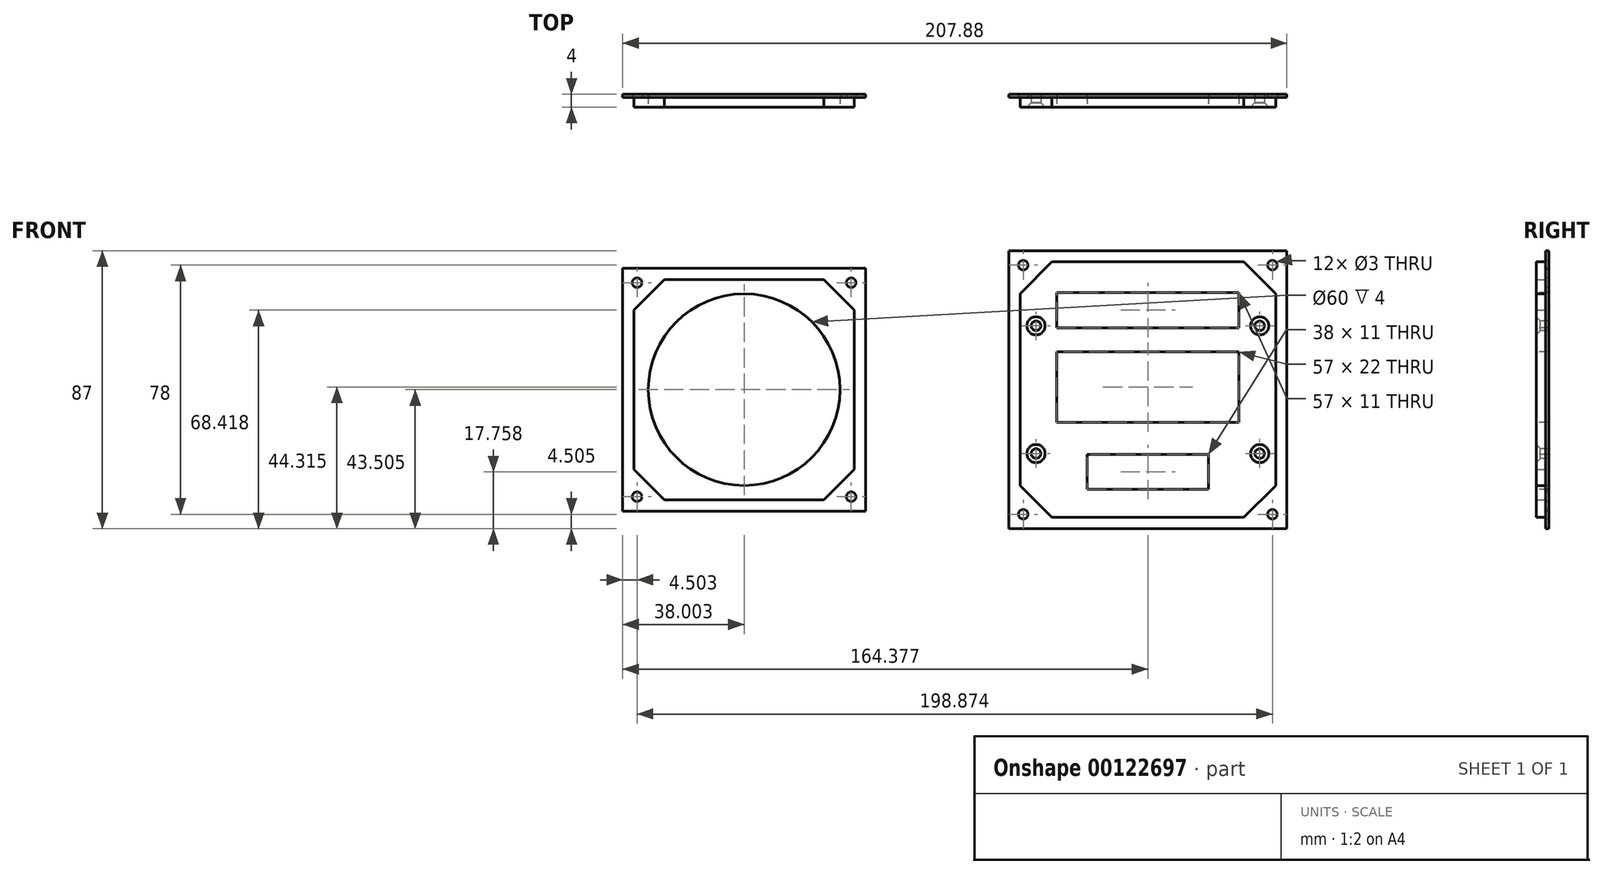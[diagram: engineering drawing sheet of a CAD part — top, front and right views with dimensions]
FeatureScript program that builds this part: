
annotation { "Feature Type Name" : "Feature", "Feature Type Description" : "" }
export const myFeature = defineFeature(function(context is Context, id is Id, definition is map)
    precondition{}
    {
        {
            var Q0;
            Q0=qCreatedBy(makeId("Front.planeOp"),FACE);
            cPlane(context, id + "F0", {"entities" : qUnion([Q0]), "cplaneType" : CPlaneType.OFFSET, "offset" : 5 * mm, "width" : 150 * mm, "height" : 150 * mm});
        }
        {
            var Q0;
            Q0=qCreatedBy(id+"F0.planeOp",FACE);
            var sketch = newSketch(context, id + "F1", { "sketchPlane" : qUnion([Q0])});
            skLineSegment(sketch, "E0.0", {"start": v(-61.26, 263.3) * mm, "end": v(-61.26, 238.3) * mm});
            skLineSegment(sketch, "E0.1", {"start": v(-61.26, 213.3) * mm, "end": v(-70.76, 203.8) * mm});
            skLineSegment(sketch, "E0.2", {"start": v(-70.76, 203.8) * mm, "end": v(-95.76, 203.8) * mm});
            skLineSegment(sketch, "E0.3", {"start": v(-120.76, 203.8) * mm, "end": v(-130.26, 213.3) * mm});
            skLineSegment(sketch, "E0.4", {"start": v(-130.26, 213.3) * mm, "end": v(-130.26, 238.3) * mm});
            skLineSegment(sketch, "E0.5", {"start": v(-130.26, 263.3) * mm, "end": v(-120.76, 272.8) * mm});
            skLineSegment(sketch, "E0.6", {"start": v(-120.76, 272.8) * mm, "end": v(-95.76, 272.8) * mm});
            skLineSegment(sketch, "E0.7", {"start": v(-70.76, 272.8) * mm, "end": v(-61.26, 263.3) * mm});
            skPoint(sketch, "E1", {"position": v(-95.76, 238.3) * mm});
            skLineSegment(sketch, "E2", {"start": v(-95.76, 272.8) * mm, "end": v(-70.76, 272.8) * mm});
            skLineSegment(sketch, "E3", {"start": v(-130.26, 238.3) * mm, "end": v(-130.26, 263.3) * mm});
            skLineSegment(sketch, "E4", {"start": v(-61.26, 238.3) * mm, "end": v(-61.26, 213.3) * mm});
            skLineSegment(sketch, "E5", {"start": v(-95.76, 203.8) * mm, "end": v(-120.76, 203.8) * mm});
            skSolve(sketch);
        }
        {
            var Q0;
            Q0=qSketchRegion(id+"F1",true);
            extrude(context, id + "F2", {"entities" : qUnion([Q0]), "depth" : 3 * mm});
        }
        {
            var Q0;
            Q0=makeQuery(id+"F2.opExtrude","CAP_FACE",FACE,{"disambiguationData":[OSD([sQuery(id+"F1.wireOp",EDGE,"E0.0"),sQuery(id+"F1.wireOp",EDGE,"E0.1"),sQuery(id+"F1.wireOp",EDGE,"E0.2"),sQuery(id+"F1.wireOp",EDGE,"E0.3"),sQuery(id+"F1.wireOp",EDGE,"E0.4"),sQuery(id+"F1.wireOp",EDGE,"E0.5"),sQuery(id+"F1.wireOp",EDGE,"E0.6"),sQuery(id+"F1.wireOp",EDGE,"E0.7"),sQuery(id+"F1.wireOp",EDGE,"E2"),sQuery(id+"F1.wireOp",EDGE,"E3"),sQuery(id+"F1.wireOp",EDGE,"E4"),sQuery(id+"F1.wireOp",EDGE,"E5")])],"isStart":true});
            var sketch = newSketch(context, id + "F3", { "sketchPlane" : qUnion([Q0])});
            skLineSegment(sketch, "E6.bottom", {"start": v(133.76, 276.3) * mm, "end": v(57.76, 276.3) * mm});
            skLineSegment(sketch, "E6.top", {"start": v(133.76, 200.3) * mm, "end": v(57.76, 200.3) * mm});
            skLineSegment(sketch, "E6.left", {"start": v(133.76, 276.3) * mm, "end": v(133.76, 200.3) * mm});
            skLineSegment(sketch, "E6.right", {"start": v(57.76, 276.3) * mm, "end": v(57.76, 200.3) * mm});
            skSolve(sketch);
        }
        {
            var Q0;
            Q0=qSketchRegion(id+"F3",true);
            extrude(context, id + "F4", {"entities" : qUnion([Q0]), "operationType" : NewBodyOperationType.ADD, "depth" : 1 * mm});
        }
        {
            var Q0;
            Q0=makeQuery(id+"F2.opExtrude","CAP_FACE",FACE,{"disambiguationData":[OSD([sQuery(id+"F1.wireOp",EDGE,"E0.0"),sQuery(id+"F1.wireOp",EDGE,"E0.1"),sQuery(id+"F1.wireOp",EDGE,"E0.2"),sQuery(id+"F1.wireOp",EDGE,"E0.3"),sQuery(id+"F1.wireOp",EDGE,"E0.4"),sQuery(id+"F1.wireOp",EDGE,"E0.5"),sQuery(id+"F1.wireOp",EDGE,"E0.6"),sQuery(id+"F1.wireOp",EDGE,"E0.7"),sQuery(id+"F1.wireOp",EDGE,"E2"),sQuery(id+"F1.wireOp",EDGE,"E3"),sQuery(id+"F1.wireOp",EDGE,"E4"),sQuery(id+"F1.wireOp",EDGE,"E5")])],"isStart":false});
            var sketch = newSketch(context, id + "F5", { "sketchPlane" : qUnion([Q0])});
            skCircle(sketch, "E7", {"center": v(-95.76, 238.3) * mm, "radius": 30 * mm});
            skCircle(sketch, "E8", {"center": v(-129.26, 271.8) * mm, "radius": 1.5 * mm});
            skCircle(sketch, "E9", {"center": v(-62.26, 271.8) * mm, "radius": 1.5 * mm});
            skCircle(sketch, "E10", {"center": v(-129.26, 204.8) * mm, "radius": 1.5 * mm});
            skCircle(sketch, "E11", {"center": v(-62.26, 204.8) * mm, "radius": 1.5 * mm});
            skSolve(sketch);
        }
        {
            var Q0;
            Q0=sQuery(id+"F5.wireOp",VERTEX,"E8.center");
            var Q1;
            Q1=sQuery(id+"F5.wireOp",VERTEX,"E9.center");
            var Q2;
            Q2=sQuery(id+"F5.wireOp",VERTEX,"E11.center");
            var Q3;
            Q3=sQuery(id+"F5.wireOp",VERTEX,"E10.center");
            var Q4;
            Q4=makeQuery(id+"F2.opExtrude","SWEPT_BODY",BODY,{"disambiguationData":[OSD([sQuery(id+"F1.wireOp",EDGE,"E0.0"),sQuery(id+"F1.wireOp",EDGE,"E0.1"),sQuery(id+"F1.wireOp",EDGE,"E0.2"),sQuery(id+"F1.wireOp",EDGE,"E0.3"),sQuery(id+"F1.wireOp",EDGE,"E0.4"),sQuery(id+"F1.wireOp",EDGE,"E0.5"),sQuery(id+"F1.wireOp",EDGE,"E0.6"),sQuery(id+"F1.wireOp",EDGE,"E0.7"),sQuery(id+"F1.wireOp",EDGE,"E2"),sQuery(id+"F1.wireOp",EDGE,"E3"),sQuery(id+"F1.wireOp",EDGE,"E4"),sQuery(id+"F1.wireOp",EDGE,"E5")])]});
            hole(context, id + "F6", {"style" : HoleStyle.SIMPLE, "endStyle" : HoleEndStyle.THROUGH, "holeDiameter" : 3 * mm, "locations" : qUnion([Q0, Q1, Q2, Q3]), "scope" : qUnion([Q4]), "isTappedThrough" : true});
        }
        {
            var Q0;
            Q0=sQuery(id+"F5.wireOp",VERTEX,"E7.center");
            var Q1;
            Q1=makeQuery(id+"F2.opExtrude","SWEPT_BODY",BODY,{"disambiguationData":[OSD([sQuery(id+"F1.wireOp",EDGE,"E0.0"),sQuery(id+"F1.wireOp",EDGE,"E0.1"),sQuery(id+"F1.wireOp",EDGE,"E0.2"),sQuery(id+"F1.wireOp",EDGE,"E0.3"),sQuery(id+"F1.wireOp",EDGE,"E0.4"),sQuery(id+"F1.wireOp",EDGE,"E0.5"),sQuery(id+"F1.wireOp",EDGE,"E0.6"),sQuery(id+"F1.wireOp",EDGE,"E0.7"),sQuery(id+"F1.wireOp",EDGE,"E2"),sQuery(id+"F1.wireOp",EDGE,"E3"),sQuery(id+"F1.wireOp",EDGE,"E4"),sQuery(id+"F1.wireOp",EDGE,"E5")])]});
            hole(context, id + "F7", {"style" : HoleStyle.SIMPLE, "endStyle" : HoleEndStyle.THROUGH, "holeDiameter" : 60 * mm, "locations" : qUnion([Q0]), "scope" : qUnion([Q1]), "isTappedThrough" : true});
        }
        {
            var Q0;
            Q0=qCreatedBy(id+"F0.planeOp",FACE);
            var sketch = newSketch(context, id + "F8", { "sketchPlane" : qUnion([Q0])});
            skLineSegment(sketch, "E12.0", {"start": v(70.62, 268.3) * mm, "end": v(70.62, 238.3) * mm});
            skLineSegment(sketch, "E12.1", {"start": v(70.62, 208.3) * mm, "end": v(60.62, 198.3) * mm});
            skLineSegment(sketch, "E12.2", {"start": v(60.62, 198.3) * mm, "end": v(30.62, 198.3) * mm});
            skLineSegment(sketch, "E12.3", {"start": v(0.62, 198.3) * mm, "end": v(-9.38, 208.3) * mm});
            skLineSegment(sketch, "E12.4", {"start": v(-9.38, 208.3) * mm, "end": v(-9.38, 238.3) * mm});
            skLineSegment(sketch, "E12.5", {"start": v(-9.38, 268.3) * mm, "end": v(0.62, 278.3) * mm});
            skLineSegment(sketch, "E12.6", {"start": v(0.62, 278.3) * mm, "end": v(30.62, 278.3) * mm});
            skLineSegment(sketch, "E12.7", {"start": v(60.62, 278.3) * mm, "end": v(70.62, 268.3) * mm});
            skPoint(sketch, "E13", {"position": v(30.62, 238.3) * mm});
            skLineSegment(sketch, "E14", {"start": v(30.62, 278.3) * mm, "end": v(60.62, 278.3) * mm});
            skLineSegment(sketch, "E15", {"start": v(-9.38, 238.3) * mm, "end": v(-9.38, 268.3) * mm});
            skLineSegment(sketch, "E16", {"start": v(70.62, 238.3) * mm, "end": v(70.62, 208.3) * mm});
            skLineSegment(sketch, "E17", {"start": v(30.62, 198.3) * mm, "end": v(0.62, 198.3) * mm});
            skSolve(sketch);
        }
        {
            var Q0;
            Q0=qSketchRegion(id+"F8",true);
            extrude(context, id + "F9", {"entities" : qUnion([Q0]), "depth" : 3 * mm});
        }
        {
            var Q0;
            Q0=makeQuery(id+"F9.opExtrude","CAP_FACE",FACE,{"disambiguationData":[OSD([sQuery(id+"F8.wireOp",EDGE,"E12.0"),sQuery(id+"F8.wireOp",EDGE,"E12.1"),sQuery(id+"F8.wireOp",EDGE,"E12.2"),sQuery(id+"F8.wireOp",EDGE,"E12.3"),sQuery(id+"F8.wireOp",EDGE,"E12.4"),sQuery(id+"F8.wireOp",EDGE,"E12.5"),sQuery(id+"F8.wireOp",EDGE,"E12.6"),sQuery(id+"F8.wireOp",EDGE,"E12.7"),sQuery(id+"F8.wireOp",EDGE,"E14"),sQuery(id+"F8.wireOp",EDGE,"E15"),sQuery(id+"F8.wireOp",EDGE,"E16"),sQuery(id+"F8.wireOp",EDGE,"E17")])],"isStart":true});
            var sketch = newSketch(context, id + "F10", { "sketchPlane" : qUnion([Q0])});
            skLineSegment(sketch, "E18.bottom", {"start": v(-74.12, 194.8) * mm, "end": v(12.88, 194.8) * mm});
            skLineSegment(sketch, "E18.top", {"start": v(-74.12, 281.8) * mm, "end": v(12.88, 281.8) * mm});
            skLineSegment(sketch, "E18.left", {"start": v(-74.12, 194.8) * mm, "end": v(-74.12, 281.8) * mm});
            skLineSegment(sketch, "E18.right", {"start": v(12.88, 194.8) * mm, "end": v(12.88, 281.8) * mm});
            skPoint(sketch, "E18.middle", {"position": v(-30.62, 238.3) * mm});
            skSolve(sketch);
        }
        {
            var Q0;
            Q0=qSketchRegion(id+"F10",true);
            extrude(context, id + "F11", {"entities" : qUnion([Q0]), "operationType" : NewBodyOperationType.ADD, "depth" : 1 * mm});
        }
        {
            var Q0;
            Q0=makeQuery(id+"F9.opExtrude","CAP_FACE",FACE,{"disambiguationData":[OSD([sQuery(id+"F8.wireOp",EDGE,"E12.0"),sQuery(id+"F8.wireOp",EDGE,"E12.1"),sQuery(id+"F8.wireOp",EDGE,"E12.2"),sQuery(id+"F8.wireOp",EDGE,"E12.3"),sQuery(id+"F8.wireOp",EDGE,"E12.4"),sQuery(id+"F8.wireOp",EDGE,"E12.5"),sQuery(id+"F8.wireOp",EDGE,"E12.6"),sQuery(id+"F8.wireOp",EDGE,"E12.7"),sQuery(id+"F8.wireOp",EDGE,"E14"),sQuery(id+"F8.wireOp",EDGE,"E15"),sQuery(id+"F8.wireOp",EDGE,"E16"),sQuery(id+"F8.wireOp",EDGE,"E17")])],"isStart":false});
            var sketch = newSketch(context, id + "F12", { "sketchPlane" : qUnion([Q0])});
            skCircle(sketch, "E19", {"center": v(30.62, 238.3) * mm, "radius": 30 * mm, "construction": true});
            skCircle(sketch, "E20", {"center": v(-8.38, 277.3) * mm, "radius": 1.5 * mm});
            skCircle(sketch, "E21", {"center": v(69.62, 277.3) * mm, "radius": 1.5 * mm});
            skCircle(sketch, "E22", {"center": v(-8.38, 199.3) * mm, "radius": 1.5 * mm});
            skCircle(sketch, "E23", {"center": v(69.62, 199.3) * mm, "radius": 1.5 * mm});
            skCircle(sketch, "E24", {"center": v(-4.38, 258.3) * mm, "radius": 1.5 * mm});
            skCircle(sketch, "E25", {"center": v(65.62, 258.3) * mm, "radius": 1.5 * mm});
            skCircle(sketch, "E26", {"center": v(-4.38, 218.3) * mm, "radius": 1.5 * mm});
            skCircle(sketch, "E27", {"center": v(65.62, 218.3) * mm, "radius": 1.5 * mm});
            skSolve(sketch);
        }
        {
            var Q0;
            Q0=sQuery(id+"F12.wireOp",VERTEX,"E20.center");
            var Q1;
            Q1=sQuery(id+"F12.wireOp",VERTEX,"E22.center");
            var Q2;
            Q2=sQuery(id+"F12.wireOp",VERTEX,"E23.center");
            var Q3;
            Q3=sQuery(id+"F12.wireOp",VERTEX,"E21.center");
            var Q4;
            Q4=makeQuery(id+"F9.opExtrude","SWEPT_BODY",BODY,{"disambiguationData":[OSD([sQuery(id+"F8.wireOp",EDGE,"E12.0"),sQuery(id+"F8.wireOp",EDGE,"E12.1"),sQuery(id+"F8.wireOp",EDGE,"E12.2"),sQuery(id+"F8.wireOp",EDGE,"E12.3"),sQuery(id+"F8.wireOp",EDGE,"E12.4"),sQuery(id+"F8.wireOp",EDGE,"E12.5"),sQuery(id+"F8.wireOp",EDGE,"E12.6"),sQuery(id+"F8.wireOp",EDGE,"E12.7"),sQuery(id+"F8.wireOp",EDGE,"E14"),sQuery(id+"F8.wireOp",EDGE,"E15"),sQuery(id+"F8.wireOp",EDGE,"E16"),sQuery(id+"F8.wireOp",EDGE,"E17")])]});
            hole(context, id + "F13", {"style" : HoleStyle.SIMPLE, "endStyle" : HoleEndStyle.THROUGH, "holeDiameter" : 3 * mm, "locations" : qUnion([Q0, Q1, Q2, Q3]), "scope" : qUnion([Q4]), "isTappedThrough" : true});
        }
        {
            var Q0;
            Q0=sQuery(id+"F12.wireOp",VERTEX,"E24.center");
            var Q1;
            Q1=sQuery(id+"F12.wireOp",VERTEX,"E26.center");
            var Q2;
            Q2=sQuery(id+"F12.wireOp",VERTEX,"E27.center");
            var Q3;
            Q3=sQuery(id+"F12.wireOp",VERTEX,"E25.center");
            var Q4;
            Q4=makeQuery(id+"F9.opExtrude","SWEPT_BODY",BODY,{"disambiguationData":[OSD([sQuery(id+"F8.wireOp",EDGE,"E12.0"),sQuery(id+"F8.wireOp",EDGE,"E12.1"),sQuery(id+"F8.wireOp",EDGE,"E12.2"),sQuery(id+"F8.wireOp",EDGE,"E12.3"),sQuery(id+"F8.wireOp",EDGE,"E12.4"),sQuery(id+"F8.wireOp",EDGE,"E12.5"),sQuery(id+"F8.wireOp",EDGE,"E12.6"),sQuery(id+"F8.wireOp",EDGE,"E12.7"),sQuery(id+"F8.wireOp",EDGE,"E14"),sQuery(id+"F8.wireOp",EDGE,"E15"),sQuery(id+"F8.wireOp",EDGE,"E16"),sQuery(id+"F8.wireOp",EDGE,"E17")])]});
            hole(context, id + "F14", {"style" : HoleStyle.C_SINK, "endStyle" : HoleEndStyle.THROUGH, "holeDiameter" : 3 * mm, "cSinkDiameter" : 5.7 * mm, "cSinkAngle" : 90 * degree, "locations" : qUnion([Q0, Q1, Q2, Q3]), "scope" : qUnion([Q4]), "isTappedThrough" : true});
        }
        {
            var Q0;
            Q0=makeQuery(id+"F12.imprint","IMPRINT",FACE,{"disambiguationData":[TD([[makeQuery(id+"F12.imprint","IMPRINT",EDGE,{"derivedFrom":sQuery(id+"F12.wireOp",EDGE,"E24")}),-1.0]])]});
            var sketch = newSketch(context, id + "F15", { "sketchPlane" : qUnion([Q0])});
            skLineSegment(sketch, "E28.bottom", {"start": v(20.12, 258.72) * mm, "end": v(3.12, 258.72) * mm, "construction": true});
            skLineSegment(sketch, "E28.top", {"start": v(20.12, 267.72) * mm, "end": v(3.12, 267.72) * mm, "construction": true});
            skLineSegment(sketch, "E28.left", {"start": v(20.12, 258.72) * mm, "end": v(20.12, 267.72) * mm, "construction": true});
            skLineSegment(sketch, "E28.right", {"start": v(3.12, 258.72) * mm, "end": v(3.12, 267.72) * mm, "construction": true});
            skPoint(sketch, "E28.middle", {"position": v(11.62, 263.22) * mm});
            skLineSegment(sketch, "E29.bottom", {"start": v(39.12, 258.72) * mm, "end": v(22.12, 258.72) * mm, "construction": true});
            skLineSegment(sketch, "E29.top", {"start": v(39.12, 267.72) * mm, "end": v(22.12, 267.72) * mm, "construction": true});
            skLineSegment(sketch, "E29.left", {"start": v(39.12, 258.72) * mm, "end": v(39.12, 267.72) * mm, "construction": true});
            skLineSegment(sketch, "E29.right", {"start": v(22.12, 258.72) * mm, "end": v(22.12, 267.72) * mm, "construction": true});
            skPoint(sketch, "E29.middle", {"position": v(30.62, 263.22) * mm});
            skLineSegment(sketch, "E30.bottom", {"start": v(58.12, 258.72) * mm, "end": v(41.12, 258.72) * mm, "construction": true});
            skLineSegment(sketch, "E30.top", {"start": v(58.12, 267.72) * mm, "end": v(41.12, 267.72) * mm, "construction": true});
            skLineSegment(sketch, "E30.left", {"start": v(58.12, 258.72) * mm, "end": v(58.12, 267.72) * mm, "construction": true});
            skLineSegment(sketch, "E30.right", {"start": v(41.12, 258.72) * mm, "end": v(41.12, 267.72) * mm, "construction": true});
            skPoint(sketch, "E30.middle", {"position": v(49.62, 263.22) * mm});
            skLineSegment(sketch, "E31.bottom", {"start": v(29.62, 208.06) * mm, "end": v(12.62, 208.06) * mm, "construction": true});
            skLineSegment(sketch, "E31.top", {"start": v(29.62, 217.06) * mm, "end": v(12.62, 217.06) * mm, "construction": true});
            skLineSegment(sketch, "E31.left", {"start": v(29.62, 208.06) * mm, "end": v(29.62, 217.06) * mm, "construction": true});
            skLineSegment(sketch, "E31.right", {"start": v(12.62, 208.06) * mm, "end": v(12.62, 217.06) * mm, "construction": true});
            skPoint(sketch, "E31.middle", {"position": v(21.12, 212.56) * mm});
            skLineSegment(sketch, "E32.bottom", {"start": v(48.62, 208.06) * mm, "end": v(31.62, 208.06) * mm, "construction": true});
            skLineSegment(sketch, "E32.top", {"start": v(48.62, 217.06) * mm, "end": v(31.62, 217.06) * mm, "construction": true});
            skLineSegment(sketch, "E32.left", {"start": v(48.62, 208.06) * mm, "end": v(48.62, 217.06) * mm, "construction": true});
            skLineSegment(sketch, "E32.right", {"start": v(31.62, 208.06) * mm, "end": v(31.62, 217.06) * mm, "construction": true});
            skPoint(sketch, "E32.middle", {"position": v(40.12, 212.56) * mm});
            skLineSegment(sketch, "E33.bottom", {"start": v(59.12, 257.72) * mm, "end": v(2.12, 257.72) * mm});
            skLineSegment(sketch, "E33.top", {"start": v(59.12, 268.72) * mm, "end": v(2.12, 268.72) * mm});
            skLineSegment(sketch, "E33.left", {"start": v(59.12, 257.72) * mm, "end": v(59.12, 268.72) * mm});
            skLineSegment(sketch, "E33.right", {"start": v(2.12, 257.72) * mm, "end": v(2.12, 268.72) * mm});
            skLineSegment(sketch, "E34.bottom", {"start": v(20.12, 240.12) * mm, "end": v(3.12, 240.12) * mm, "construction": true});
            skLineSegment(sketch, "E34.top", {"start": v(20.12, 249.12) * mm, "end": v(3.12, 249.12) * mm, "construction": true});
            skLineSegment(sketch, "E34.left", {"start": v(20.12, 240.12) * mm, "end": v(20.12, 249.12) * mm, "construction": true});
            skLineSegment(sketch, "E34.right", {"start": v(3.12, 240.12) * mm, "end": v(3.12, 249.12) * mm, "construction": true});
            skPoint(sketch, "E34.middle", {"position": v(11.62, 244.62) * mm});
            skLineSegment(sketch, "E35.bottom", {"start": v(39.12, 240.12) * mm, "end": v(22.12, 240.12) * mm, "construction": true});
            skLineSegment(sketch, "E35.top", {"start": v(39.12, 249.12) * mm, "end": v(22.12, 249.12) * mm, "construction": true});
            skLineSegment(sketch, "E35.left", {"start": v(39.12, 240.12) * mm, "end": v(39.12, 249.12) * mm, "construction": true});
            skLineSegment(sketch, "E35.right", {"start": v(22.12, 240.12) * mm, "end": v(22.12, 249.12) * mm, "construction": true});
            skPoint(sketch, "E35.middle", {"position": v(30.62, 244.62) * mm});
            skLineSegment(sketch, "E36.bottom", {"start": v(58.12, 240.12) * mm, "end": v(41.12, 240.12) * mm, "construction": true});
            skLineSegment(sketch, "E36.top", {"start": v(58.12, 249.12) * mm, "end": v(41.12, 249.12) * mm, "construction": true});
            skLineSegment(sketch, "E36.left", {"start": v(58.12, 240.12) * mm, "end": v(58.12, 249.12) * mm, "construction": true});
            skLineSegment(sketch, "E36.right", {"start": v(41.12, 240.12) * mm, "end": v(41.12, 249.12) * mm, "construction": true});
            skPoint(sketch, "E36.middle", {"position": v(49.62, 244.62) * mm});
            skLineSegment(sketch, "E37.top", {"start": v(20.12, 238.12) * mm, "end": v(3.12, 238.12) * mm, "construction": true});
            skLineSegment(sketch, "E37.left", {"start": v(20.12, 229.12) * mm, "end": v(20.12, 238.12) * mm, "construction": true});
            skLineSegment(sketch, "E37.right", {"start": v(3.12, 229.12) * mm, "end": v(3.12, 238.12) * mm, "construction": true});
            skPoint(sketch, "E37.middle", {"position": v(11.62, 233.62) * mm});
            skLineSegment(sketch, "E38.bottom", {"start": v(39.12, 229.12) * mm, "end": v(22.12, 229.12) * mm, "construction": true});
            skLineSegment(sketch, "E38.top", {"start": v(39.12, 238.12) * mm, "end": v(22.12, 238.12) * mm, "construction": true});
            skLineSegment(sketch, "E38.left", {"start": v(39.12, 229.12) * mm, "end": v(39.12, 238.12) * mm, "construction": true});
            skLineSegment(sketch, "E38.right", {"start": v(22.12, 229.12) * mm, "end": v(22.12, 238.12) * mm, "construction": true});
            skPoint(sketch, "E38.middle", {"position": v(30.62, 233.62) * mm});
            skLineSegment(sketch, "E39.bottom", {"start": v(58.12, 229.12) * mm, "end": v(41.12, 229.12) * mm, "construction": true});
            skLineSegment(sketch, "E39.top", {"start": v(58.12, 238.12) * mm, "end": v(41.12, 238.12) * mm, "construction": true});
            skLineSegment(sketch, "E39.left", {"start": v(58.12, 229.12) * mm, "end": v(58.12, 238.12) * mm, "construction": true});
            skLineSegment(sketch, "E39.right", {"start": v(41.12, 229.12) * mm, "end": v(41.12, 238.12) * mm, "construction": true});
            skPoint(sketch, "E39.middle", {"position": v(49.62, 233.62) * mm});
            skLineSegment(sketch, "E40", {"start": v(3.12, 229.12) * mm, "end": v(20.12, 229.12) * mm, "construction": true});
            skLineSegment(sketch, "E41.bottom", {"start": v(2.12, 250.12) * mm, "end": v(59.12, 250.12) * mm});
            skLineSegment(sketch, "E41.top", {"start": v(2.12, 228.12) * mm, "end": v(59.12, 228.12) * mm});
            skLineSegment(sketch, "E41.left", {"start": v(2.12, 250.12) * mm, "end": v(2.12, 228.12) * mm});
            skLineSegment(sketch, "E41.right", {"start": v(59.12, 250.12) * mm, "end": v(59.12, 228.12) * mm});
            skLineSegment(sketch, "E42.bottom", {"start": v(11.62, 218.06) * mm, "end": v(49.62, 218.06) * mm});
            skLineSegment(sketch, "E42.top", {"start": v(11.62, 207.06) * mm, "end": v(49.62, 207.06) * mm});
            skLineSegment(sketch, "E42.left", {"start": v(11.62, 218.06) * mm, "end": v(11.62, 207.06) * mm});
            skLineSegment(sketch, "E42.right", {"start": v(49.62, 218.06) * mm, "end": v(49.62, 207.06) * mm});
            skSolve(sketch);
        }
        {
            var Q0;
            Q0=qSketchRegion(id+"F15",true);
            extrude(context, id + "F16", {"entities" : qUnion([Q0]), "operationType" : NewBodyOperationType.REMOVE, "oppositeDirection" : true, "depth" : 5 * mm});
        }
    });
